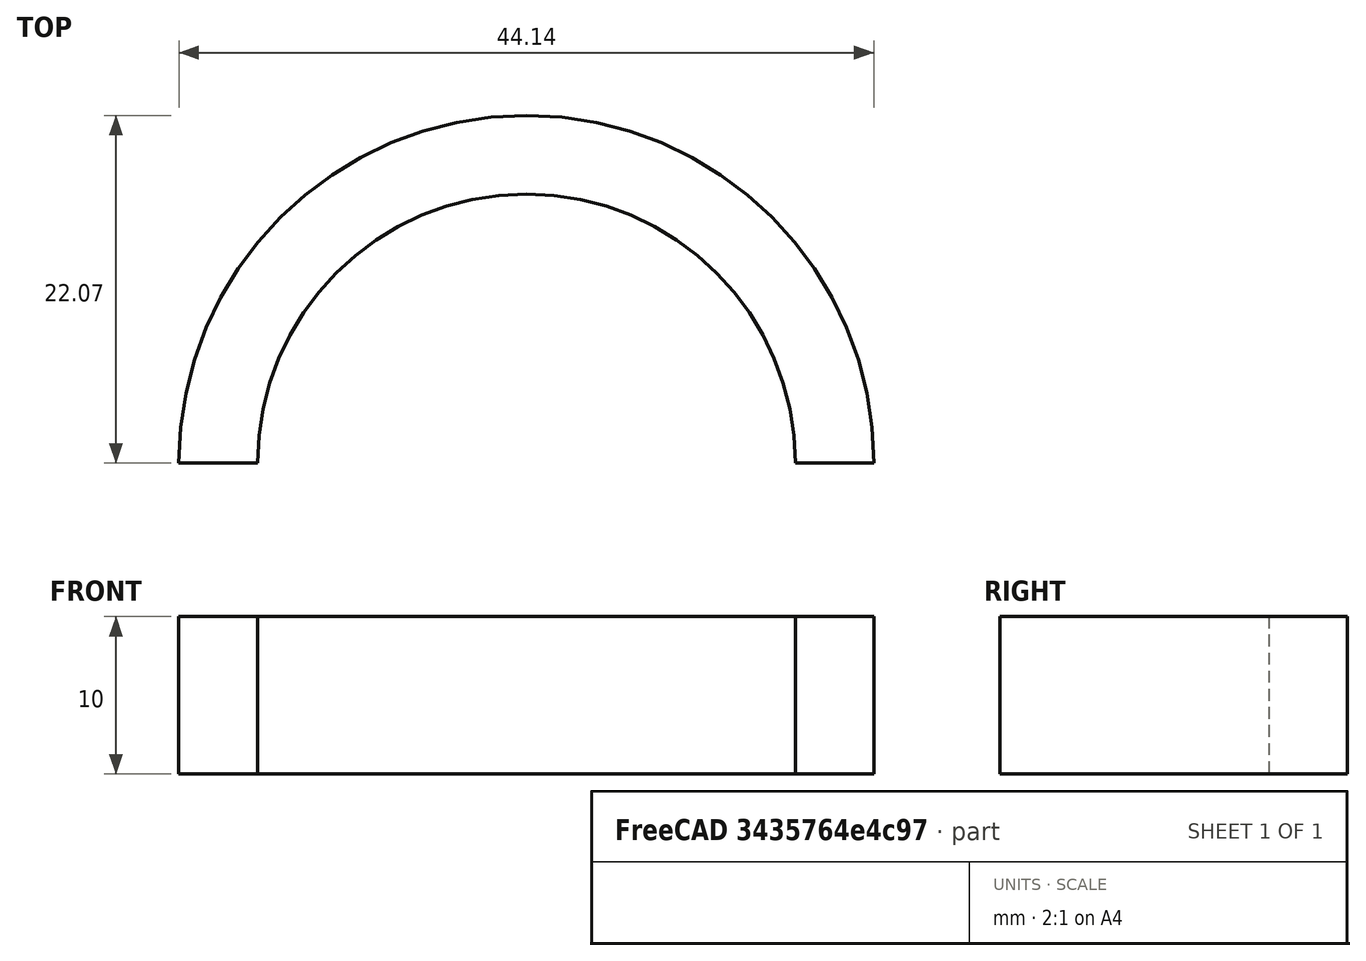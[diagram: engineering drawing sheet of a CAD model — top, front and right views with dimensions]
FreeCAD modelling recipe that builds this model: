
FCSTD DOCUMENT  (FreeCAD 0.20R29177 (Git))
Label: YawBearing_ArcWireSupport
License: All rights reserved
LicenseURL: http://en.wikipedia.org/wiki/All_rights_reserved
objects: Sketcher::SketchObject×1, PartDesign::Pad×1, PartDesign::Body×1, Spreadsheet::Sheet×1
note: 4 computed .brp shape members not serialized (recipe doc carries the construction recipe); baked Part::Feature solids carry a one-line shape summary decoded from their .brp
EXTERNAL_REF file=../Master_of_Puppets.FCStd obj=YawBearing

FEATURE [Sketcher::SketchObject] Sketch
  FullyConstrained = true
  MapMode = 5
  Support = -> [XY_Plane001]
  expr: Constraints[8] = Spreadsheet.ArcWireSupportThickness
  expr: Constraints[9] = Spreadsheet.ArcWireSupportLength / 2
  sketch-geometry (4):
    g0: ArcOfCircle CenterX=0 CenterY=0 CenterZ=0 NormalX=0 NormalY=0 NormalZ=1 AngleXU=0 Radius=17.075 StartAngle=-9e-16 EndAngle=3.14159
    g1: ArcOfCircle CenterX=-1e-16 CenterY=0 CenterZ=0 NormalX=0 NormalY=0 NormalZ=1 AngleXU=0 Radius=22.075 StartAngle=-8.9e-15 EndAngle=3.14159
    g2: LineSegment StartX=-22.075 StartY=6.9728e-12 StartZ=0 EndX=-17.075 EndY=-1.268e-13 EndZ=0
    g3: LineSegment StartX=17.075 StartY=-1.52e-14 StartZ=0 EndX=22.075 EndY=-1.961e-13 EndZ=0
  constraints (12):
    c: Coincident(g0,g-1)
    c: PointOnObject(g0,g-1)
    c: PointOnObject(g0,g-1)
    c: Coincident(g1,g-1)
    c: PointOnObject(g1,g-1)
    c: Coincident(g2,g1)
    c: Coincident(g2,g0)
    c: Coincident(g3,g1)
    c: DistanceX(g2,g2) = 5
    c: DistanceX(g-2,g1) = 22.075
    c: Coincident(g0,g3)
    c: PointOnObject(g1,g-1)
FEATURE [PartDesign::Pad] Pad
  AllowMultiFace = false
  Direction = (0,0,1)
  Length = 10
  Length2 = 100
  Midplane = true
  Profile = -> Sketch
  Type = 0
  expr: Length = Spreadsheet.ArcWireSupportWidth
FEATURE [PartDesign::Body] PadBody  label="ArcWireSupport"
  Group = -> [Sketch,Pad]
  Origin = -> Origin001
  Tip = -> Pad
FEATURE [Spreadsheet::Sheet] Spreadsheet
  cells = A1=Inputs; A2=ArcWireSupportThickness; B2(ArcWireSupportThickness)==Master_of_Puppets#YawBearing.ArcWireSupportThickness; A3=ArcWireSupportWidth; B3(ArcWireSupportWidth)==Master_of_Puppets#YawBearing.ArcWireSupportWidth; A4=ArcWireSupportLength; B4(ArcWireSupportLength)==Master_of_Puppets#YawBearing.ArcWireSupportLength
